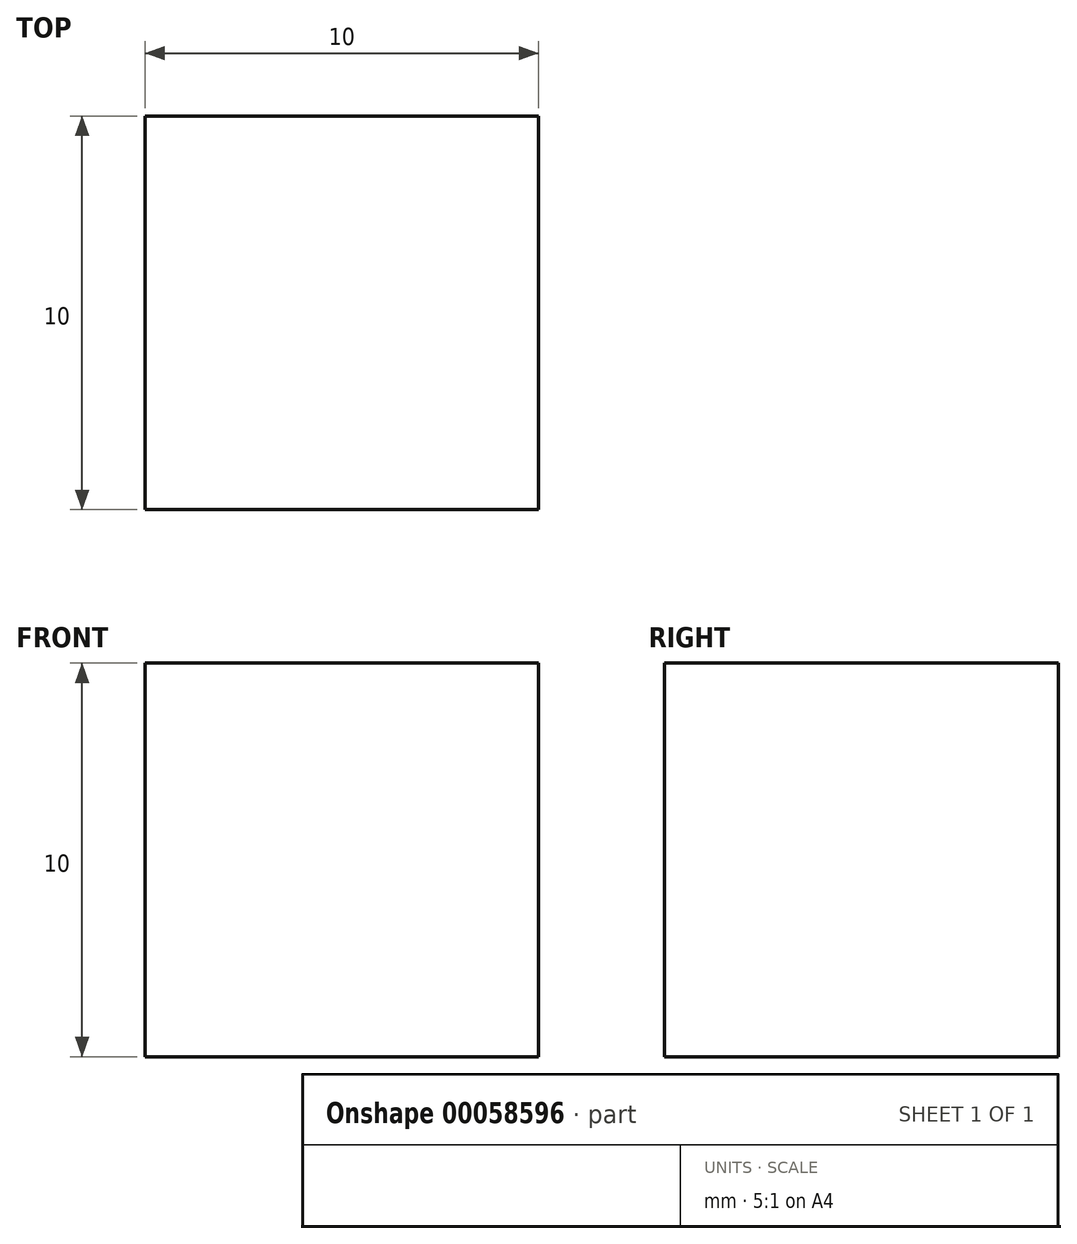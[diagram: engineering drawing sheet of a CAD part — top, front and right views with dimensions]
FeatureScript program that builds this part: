
annotation { "Feature Type Name" : "Feature", "Feature Type Description" : "" }
export const myFeature = defineFeature(function(context is Context, id is Id, definition is map)
    precondition{}
    {
        {
            var Q0;
            Q0=qCreatedBy(makeId("Top.planeOp"),FACE);
            var sketch = newSketch(context, id + "F0", { "sketchPlane" : qUnion([Q0])});
            skLineSegment(sketch, "E0.rect.bottom", {"start": v(5, 5) * mm, "end": v(-5, 5) * mm});
            skLineSegment(sketch, "E0.rect.top", {"start": v(5, -5) * mm, "end": v(-5, -5) * mm});
            skLineSegment(sketch, "E0.rect.left", {"start": v(5, 5) * mm, "end": v(5, -5) * mm});
            skLineSegment(sketch, "E0.rect.right", {"start": v(-5, 5) * mm, "end": v(-5, -5) * mm});
            skPoint(sketch, "E0.rect.middle", {"position": v(0, 0) * mm});
            skSolve(sketch);
        }
        {
            var Q0;
            Q0 = qSketchRegion(id + "F0", true);
            extrude(context, id + "F1", {"entities" : qUnion([Q0]), "depth" : 10 * mm});
        }
    });
